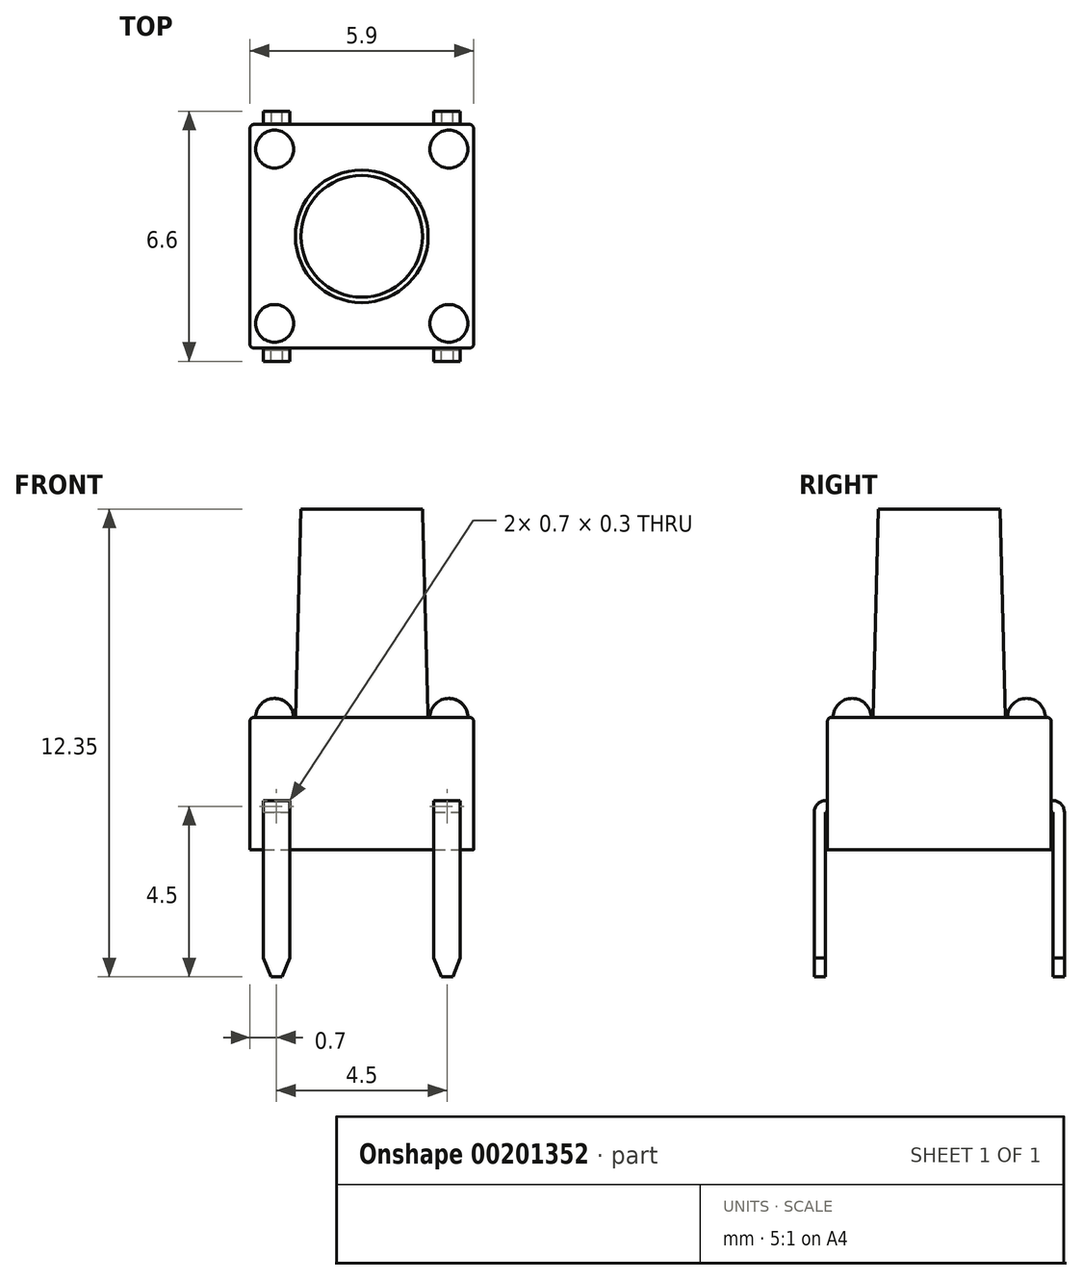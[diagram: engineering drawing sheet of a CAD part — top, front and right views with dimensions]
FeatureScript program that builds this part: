
annotation { "Feature Type Name" : "Feature", "Feature Type Description" : "" }
export const myFeature = defineFeature(function(context is Context, id is Id, definition is map)
    precondition{}
    {
        {
            var Q0;
            Q0=qCreatedBy(makeId("Top.planeOp"),FACE);
            var sketch = newSketch(context, id + "F0", { "sketchPlane" : qUnion([Q0])});
            skLineSegment(sketch, "E0.bottom", {"start": v(-2.95, 2.95) * mm, "end": v(2.95, 2.95) * mm});
            skLineSegment(sketch, "E0.top", {"start": v(-2.95, -2.95) * mm, "end": v(2.95, -2.95) * mm});
            skLineSegment(sketch, "E0.left", {"start": v(-2.95, 2.95) * mm, "end": v(-2.95, -2.95) * mm});
            skLineSegment(sketch, "E0.right", {"start": v(2.95, 2.95) * mm, "end": v(2.95, -2.95) * mm});
            skSolve(sketch);
        }
        {
            var Q0;
            Q0=makeQuery(id+"F0.imprint","IMPRINT",FACE,{"disambiguationData":[TD([[makeQuery(id+"F0.imprint","IMPRINT",EDGE,{"derivedFrom":sQuery(id+"F0.wireOp",EDGE,"E0.bottom")}),-1.0]])]});
            extrude(context, id + "F1", {"entities" : qUnion([Q0]), "depth" : 3.5 * mm});
        }
        {
            var Q0;
            Q0=makeQuery(id+"F1.opExtrude","CAP_FACE",FACE,{"disambiguationData":[OSD([sQuery(id+"F0.wireOp",EDGE,"E0.bottom"),sQuery(id+"F0.wireOp",EDGE,"E0.top"),sQuery(id+"F0.wireOp",EDGE,"E0.left"),sQuery(id+"F0.wireOp",EDGE,"E0.right")])],"isStart":false});
            var sketch = newSketch(context, id + "F2", { "sketchPlane" : qUnion([Q0])});
            skCircle(sketch, "E1", {"center": v(0, 0) * mm, "radius": 1.75 * mm});
            skSolve(sketch);
        }
        {
            var Q0;
            Q0 = qSketchRegion(id + "F2", true);
            extrude(context, id + "F3", {"entities" : qUnion([Q0]), "operationType" : NewBodyOperationType.ADD, "depth" : 5.5 * mm, "hasDraft" : true, "draftAngle" : 1.5 * degree, "draftPullDirection" : true});
        }
        {
            var Q0;
            Q0=makeQuery(id+"F1.opExtrude","SWEPT_EDGE",EDGE,{"disambiguationData":[OSD([sQuery(id+"F0.wireOp",EDGE,"E0.top"),sQuery(id+"F0.wireOp",EDGE,"E0.right")])]});
            var Q1;
            Q1=makeQuery(id+"F1.opExtrude","SWEPT_EDGE",EDGE,{"disambiguationData":[OSD([sQuery(id+"F0.wireOp",EDGE,"E0.top"),sQuery(id+"F0.wireOp",EDGE,"E0.left")])]});
            var Q2;
            Q2=makeQuery(id+"F1.opExtrude","SWEPT_EDGE",EDGE,{"disambiguationData":[OSD([sQuery(id+"F0.wireOp",EDGE,"E0.bottom"),sQuery(id+"F0.wireOp",EDGE,"E0.left")])]});
            var Q3;
            Q3=makeQuery(id+"F1.opExtrude","SWEPT_EDGE",EDGE,{"disambiguationData":[OSD([sQuery(id+"F0.wireOp",EDGE,"E0.bottom"),sQuery(id+"F0.wireOp",EDGE,"E0.right")])]});
            var Q4;
            Q4=makeQuery(id+"F1.opExtrude","CAP_EDGE",EDGE,{"disambiguationData":[OSD([sQuery(id+"F0.wireOp",EDGE,"E0.right")])],"isStart":false});
            var Q5;
            Q5=makeQuery(id+"F1.opExtrude","CAP_EDGE",EDGE,{"disambiguationData":[OSD([sQuery(id+"F0.wireOp",EDGE,"E0.top")])],"isStart":false});
            var Q6;
            Q6=makeQuery(id+"F1.opExtrude","CAP_EDGE",EDGE,{"disambiguationData":[OSD([sQuery(id+"F0.wireOp",EDGE,"E0.left")])],"isStart":false});
            var Q7;
            Q7=makeQuery(id+"F1.opExtrude","CAP_EDGE",EDGE,{"disambiguationData":[OSD([sQuery(id+"F0.wireOp",EDGE,"E0.bottom")])],"isStart":false});
            fillet(context, id + "F4", {"entities" : qUnion([Q0, Q1, Q2, Q3, Q4, Q5, Q6, Q7]), "radius" : 0.1 * mm, "tangentPropagation" : true, "allowEdgeOverflow" : false});
        }
        {
            var Q0;
            Q0=makeQuery(id+"F1.opExtrude","CAP_FACE",FACE,{"disambiguationData":[OSD([sQuery(id+"F0.wireOp",EDGE,"E0.bottom"),sQuery(id+"F0.wireOp",EDGE,"E0.top"),sQuery(id+"F0.wireOp",EDGE,"E0.left"),sQuery(id+"F0.wireOp",EDGE,"E0.right")])],"isStart":false});
            var sketch = newSketch(context, id + "F5", { "sketchPlane" : qUnion([Q0])});
            skCircle(sketch, "E2", {"center": v(2.3, 2.3) * mm, "radius": 0.5 * mm});
            skCircle(sketch, "E3", {"center": v(2.3, -2.3) * mm, "radius": 0.5 * mm});
            skCircle(sketch, "E4", {"center": v(-2.3, -2.3) * mm, "radius": 0.5 * mm});
            skCircle(sketch, "E5", {"center": v(-2.3, 2.3) * mm, "radius": 0.5 * mm});
            skLineSegment(sketch, "E6", {"start": v(0, -2.85) * mm, "end": v(0, 2.85) * mm, "construction": true});
            skLineSegment(sketch, "E7", {"start": v(2.85, 0) * mm, "end": v(-2.85, 0) * mm, "construction": true});
            skSolve(sketch);
        }
        {
            var Q0;
            Q0=makeQuery(id+"F5.imprint","IMPRINT",FACE,{"disambiguationData":[TD([[makeQuery(id+"F5.imprint","IMPRINT",EDGE,{"derivedFrom":sQuery(id+"F5.wireOp",EDGE,"E3")}),1.0]])]});
            var Q1;
            Q1=makeQuery(id+"F5.imprint","IMPRINT",FACE,{"disambiguationData":[TD([[makeQuery(id+"F5.imprint","IMPRINT",EDGE,{"derivedFrom":sQuery(id+"F5.wireOp",EDGE,"E2")}),1.0]])]});
            var Q2;
            Q2=makeQuery(id+"F5.imprint","IMPRINT",FACE,{"disambiguationData":[TD([[makeQuery(id+"F5.imprint","IMPRINT",EDGE,{"derivedFrom":sQuery(id+"F5.wireOp",EDGE,"E5")}),1.0]])]});
            var Q3;
            Q3=makeQuery(id+"F5.imprint","IMPRINT",FACE,{"disambiguationData":[TD([[makeQuery(id+"F5.imprint","IMPRINT",EDGE,{"derivedFrom":sQuery(id+"F5.wireOp",EDGE,"E4")}),1.0]])]});
            extrude(context, id + "F6", {"entities" : qUnion([Q0, Q1, Q2, Q3]), "operationType" : NewBodyOperationType.ADD, "offsetDistance" : 25 * mm, "depth" : 0.5 * mm});
        }
        {
            var Q0;
            Q0=makeQuery(id+"F6.opExtrude","CAP_EDGE",EDGE,{"disambiguationData":[OSD([sQuery(id+"F5.wireOp",EDGE,"E3")])],"isStart":false});
            var Q1;
            Q1=makeQuery(id+"F6.opExtrude","CAP_EDGE",EDGE,{"disambiguationData":[OSD([sQuery(id+"F5.wireOp",EDGE,"E2")])],"isStart":false});
            var Q2;
            Q2=makeQuery(id+"F6.opExtrude","CAP_EDGE",EDGE,{"disambiguationData":[OSD([sQuery(id+"F5.wireOp",EDGE,"E5")])],"isStart":false});
            var Q3;
            Q3=makeQuery(id+"F6.opExtrude","CAP_EDGE",EDGE,{"disambiguationData":[OSD([sQuery(id+"F5.wireOp",EDGE,"E4")])],"isStart":false});
            fillet(context, id + "F7", {"entities" : qUnion([Q0, Q1, Q2, Q3]), "radius" : 0.5 * mm, "tangentPropagation" : true, "allowEdgeOverflow" : false});
        }
        {
            var Q0;
            Q0=makeQuery(id+"F1.opExtrude","SWEPT_FACE",FACE,{"disambiguationData":[OSD([sQuery(id+"F0.wireOp",EDGE,"E0.top")])]});
            var sketch = newSketch(context, id + "F8", { "sketchPlane" : qUnion([Q0])});
            skLineSegment(sketch, "E8.bottom", {"start": v(-2.6, 1.3) * mm, "end": v(-1.9, 1.3) * mm});
            skLineSegment(sketch, "E8.top", {"start": v(-2.6, 1) * mm, "end": v(-1.9, 1) * mm});
            skLineSegment(sketch, "E8.left", {"start": v(-2.6, 1.3) * mm, "end": v(-2.6, 1) * mm});
            skLineSegment(sketch, "E8.right", {"start": v(-1.9, 1.3) * mm, "end": v(-1.9, 1) * mm});
            skLineSegment(sketch, "E9.bottom", {"start": v(1.9, 1.3) * mm, "end": v(2.6, 1.3) * mm});
            skLineSegment(sketch, "E9.top", {"start": v(1.9, 1) * mm, "end": v(2.6, 1) * mm});
            skLineSegment(sketch, "E9.left", {"start": v(1.9, 1.3) * mm, "end": v(1.9, 1) * mm});
            skLineSegment(sketch, "E9.right", {"start": v(2.6, 1.3) * mm, "end": v(2.6, 1) * mm});
            skLineSegment(sketch, "E10", {"start": v(0, 3.4) * mm, "end": v(0, 0) * mm, "construction": true});
            skSolve(sketch);
        }
        {
            var Q0;
            Q0=qCreatedBy(makeId("Right.planeOp"),FACE);
            var sketch = newSketch(context, id + "F9", { "sketchPlane" : qUnion([Q0])});
            skLineSegment(sketch, "E11", {"start": v(-2.95, 1.15) * mm, "end": v(-3, 1.15) * mm});
            skLineSegment(sketch, "E12", {"start": v(-2.95, 1.58) * mm, "end": v(-2.95, 0.7) * mm, "construction": true});
            skLineSegment(sketch, "E13", {"start": v(-3.15, 1) * mm, "end": v(-3.15, -3.35) * mm});
            skPoint(sketch, "E14.visualSharp", {"position": v(-3.15, 1.15) * mm});
            skArc(sketch, "E14.filletArc", {"start": v(-3, 1.15) * mm, "mid": v(-3.1, 1.1) * mm, "end": v(-3.15, 1) * mm});
            skSolve(sketch);
        }
        {
            var Q0;
            Q0=makeQuery(id+"F8.imprint","IMPRINT",FACE,{"disambiguationData":[TD([[makeQuery(id+"F8.imprint","IMPRINT",EDGE,{"derivedFrom":sQuery(id+"F8.wireOp",EDGE,"E8.bottom")}),-1.0]])]});
            var Q1;
            Q1=makeQuery(id+"F8.imprint","IMPRINT",FACE,{"disambiguationData":[TD([[makeQuery(id+"F8.imprint","IMPRINT",EDGE,{"derivedFrom":sQuery(id+"F8.wireOp",EDGE,"E9.bottom")}),-1.0]])]});
            var Q2;
            Q2=sQuery(id+"F9.wireOp",EDGE,"E11");
            var Q3;
            Q3=sQuery(id+"F9.wireOp",EDGE,"E14.filletArc");
            var Q4;
            Q4=sQuery(id+"F9.wireOp",EDGE,"E13");
            sweep(context, id + "F10", {"profiles" : qUnion([Q0, Q1]), "path" : qUnion([Q2, Q3, Q4])});
        }
        {
            var Q0;
            Q0=makeQuery(id+"F10.opSweep","CAP_EDGE",EDGE,{"disambiguationData":[OSD([sQuery(id+"F8.wireOp",EDGE,"E8.left"),sQuery(id+"F9.wireOp",VERTEX,"E13.end")])],"isStart":false});
            var Q1;
            Q1=makeQuery(id+"F10.opSweep","CAP_EDGE",EDGE,{"disambiguationData":[OSD([sQuery(id+"F8.wireOp",EDGE,"E8.right"),sQuery(id+"F9.wireOp",VERTEX,"E13.end")])],"isStart":false});
            var Q2;
            Q2=makeQuery(id+"F10.opSweep","CAP_EDGE",EDGE,{"disambiguationData":[OSD([sQuery(id+"F8.wireOp",EDGE,"E9.left"),sQuery(id+"F9.wireOp",VERTEX,"E13.end")])],"isStart":false});
            var Q3;
            Q3=makeQuery(id+"F10.opSweep","CAP_EDGE",EDGE,{"disambiguationData":[OSD([sQuery(id+"F8.wireOp",EDGE,"E9.right"),sQuery(id+"F9.wireOp",VERTEX,"E13.end")])],"isStart":false});
            chamfer(context, id + "F11", {"entities" : qUnion([Q0, Q1, Q2, Q3]), "chamferType" : ChamferType.TWO_OFFSETS, "width1" : 0.2 * mm, "oppositeDirection" : false, "width2" : 0.5 * mm, "tangentPropagation" : true});
        }
        {
            var Q0;
            Q0=makeQuery(id+"F10.opSweep","SWEPT_BODY",BODY,{"disambiguationData":[OSD([sQuery(id+"F8.wireOp",EDGE,"E9.bottom"),sQuery(id+"F8.wireOp",EDGE,"E9.top"),sQuery(id+"F8.wireOp",EDGE,"E9.left"),sQuery(id+"F8.wireOp",EDGE,"E9.right"),sQuery(id+"F9.wireOp",EDGE,"E13")])]});
            var Q1;
            Q1=makeQuery(id+"F10.opSweep","SWEPT_BODY",BODY,{"disambiguationData":[OSD([sQuery(id+"F8.wireOp",EDGE,"E8.bottom"),sQuery(id+"F8.wireOp",EDGE,"E8.top"),sQuery(id+"F8.wireOp",EDGE,"E8.left"),sQuery(id+"F8.wireOp",EDGE,"E8.right"),sQuery(id+"F9.wireOp",EDGE,"E13")])]});
            var Q2;
            Q2=qCreatedBy(makeId("Front.planeOp"),FACE);
            mirror(context, id + "F12", {"operationType" : NewBodyOperationType.ADD, "entities" : qUnion([Q0, Q1]), "mirrorPlane" : qUnion([Q2])});
        }
    });
